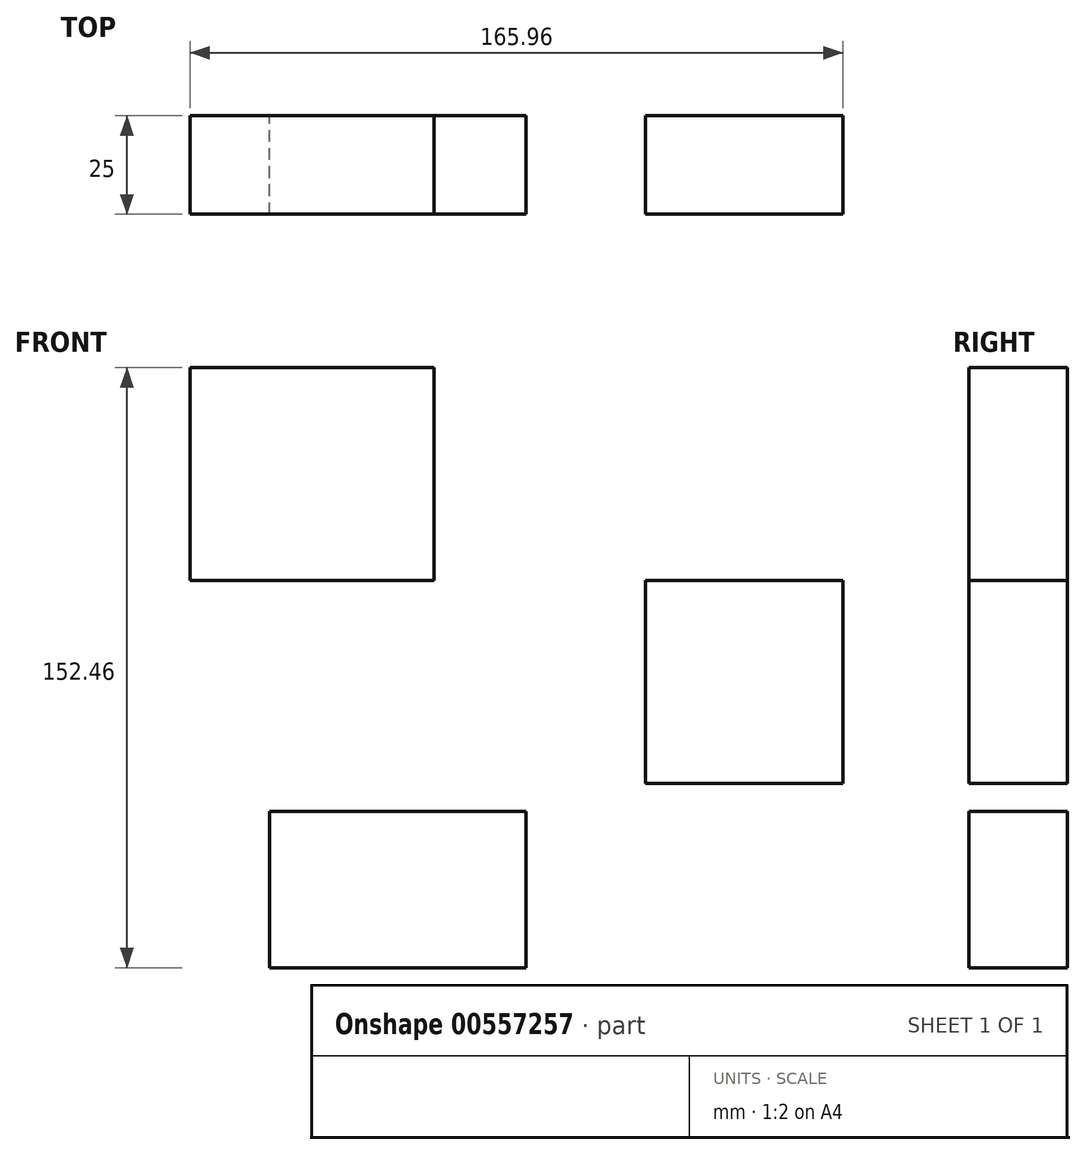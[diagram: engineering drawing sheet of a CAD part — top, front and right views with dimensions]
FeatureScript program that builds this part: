
annotation { "Feature Type Name" : "Feature", "Feature Type Description" : "" }
export const myFeature = defineFeature(function(context is Context, id is Id, definition is map)
    precondition{}
    {
        {
            var Q0;
            Q0=qCreatedBy(makeId("Front.planeOp"),FACE);
            var sketch = newSketch(context, id + "F0", { "sketchPlane" : qUnion([Q0])});
            skLineSegment(sketch, "E0.bottom", {"start": v(-69.17, 54.02) * mm, "end": v(-7.1, 54.02) * mm});
            skLineSegment(sketch, "E0.top", {"start": v(-69.17, 0) * mm, "end": v(-7.1, 0) * mm});
            skLineSegment(sketch, "E0.left", {"start": v(-69.17, 54.02) * mm, "end": v(-69.17, 0) * mm});
            skLineSegment(sketch, "E0.right", {"start": v(-7.1, 54.02) * mm, "end": v(-7.1, 0) * mm});
            skLineSegment(sketch, "E1.bottom", {"start": v(46.62, 0) * mm, "end": v(96.8, 0) * mm});
            skLineSegment(sketch, "E1.top", {"start": v(46.62, -51.62) * mm, "end": v(96.8, -51.62) * mm});
            skLineSegment(sketch, "E1.left", {"start": v(46.62, 0) * mm, "end": v(46.62, -51.62) * mm});
            skLineSegment(sketch, "E1.right", {"start": v(96.8, 0) * mm, "end": v(96.8, -51.62) * mm});
            skLineSegment(sketch, "E2.bottom", {"start": v(-48.9, -58.71) * mm, "end": v(16.22, -58.71) * mm});
            skLineSegment(sketch, "E2.top", {"start": v(-48.9, -98.44) * mm, "end": v(16.22, -98.44) * mm});
            skLineSegment(sketch, "E2.left", {"start": v(-48.9, -58.71) * mm, "end": v(-48.9, -98.44) * mm});
            skLineSegment(sketch, "E2.right", {"start": v(16.22, -58.71) * mm, "end": v(16.22, -98.44) * mm});
            skSolve(sketch);
        }
        {
            var Q0;
            Q0 = qSketchRegion(id + "F0", true);
            extrude(context, id + "F1", {"entities" : qUnion([Q0]), "depth" : 25 * mm, "offsetDistance" : 25 * mm});
        }
    });
